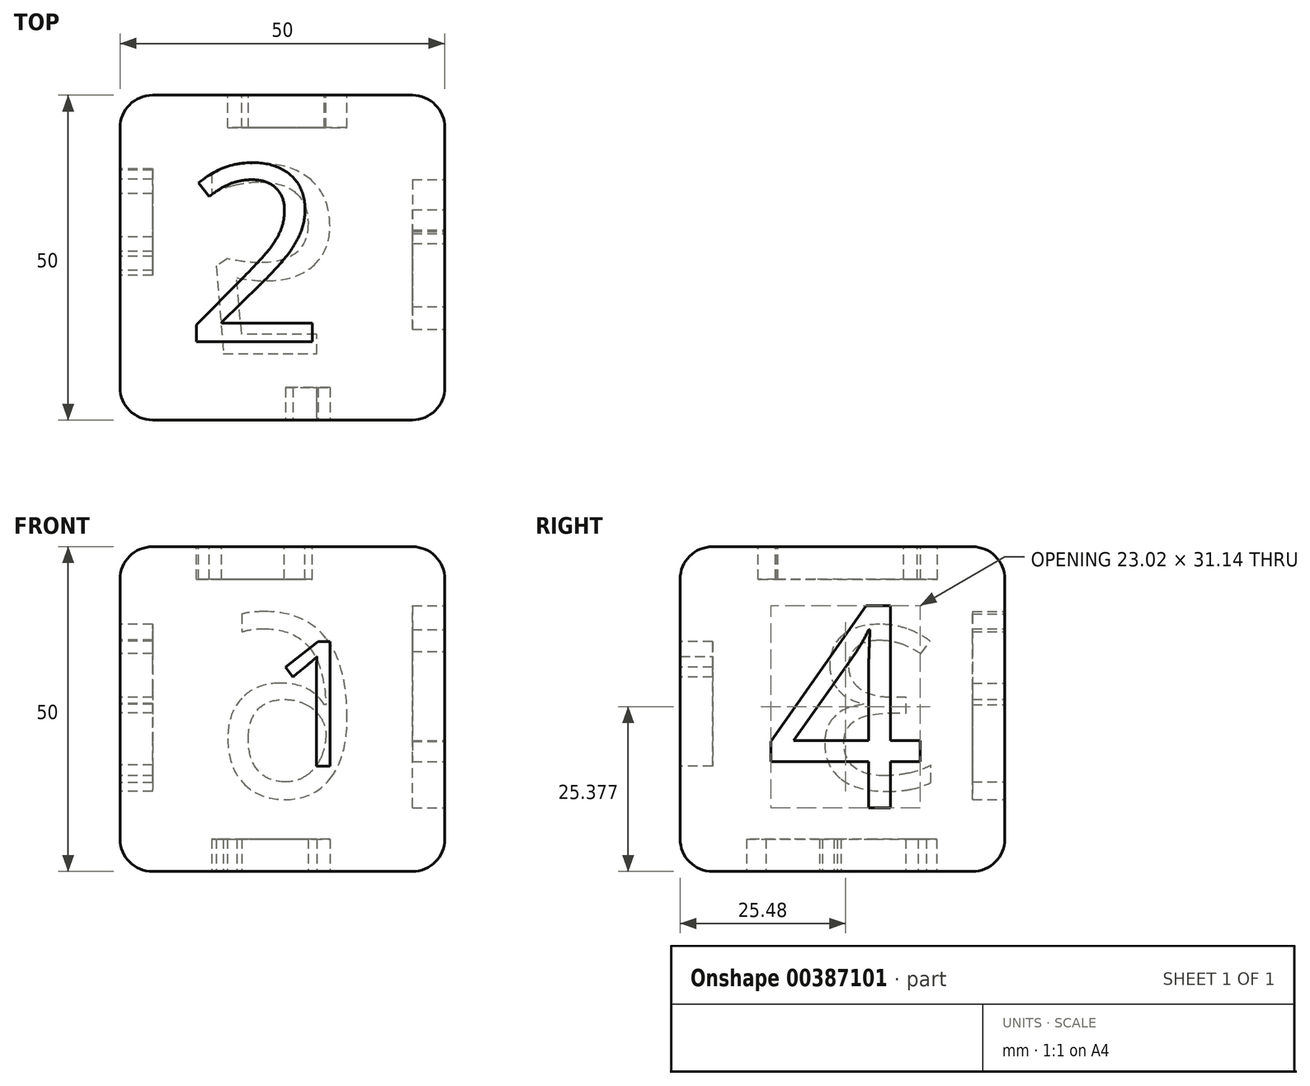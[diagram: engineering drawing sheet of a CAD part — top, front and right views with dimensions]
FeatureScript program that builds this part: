
annotation { "Feature Type Name" : "Feature", "Feature Type Description" : "" }
export const myFeature = defineFeature(function(context is Context, id is Id, definition is map)
    precondition{}
    {
        {
            var Q0;
            Q0=qCreatedBy(makeId("Front.planeOp"),FACE);
            var sketch = newSketch(context, id + "F0", { "sketchPlane" : qUnion([Q0])});
            skLineSegment(sketch, "E0.bottom", {"start": v(-34.08, 35.65) * mm, "end": v(15.92, 35.65) * mm});
            skLineSegment(sketch, "E0.top", {"start": v(-34.08, -14.35) * mm, "end": v(15.92, -14.35) * mm});
            skLineSegment(sketch, "E0.left", {"start": v(-34.08, 35.65) * mm, "end": v(-34.08, -14.35) * mm});
            skLineSegment(sketch, "E0.right", {"start": v(15.92, 35.65) * mm, "end": v(15.92, -14.35) * mm});
            skSolve(sketch);
        }
        {
            var Q0;
            Q0=makeQuery(id+"F0.imprint","IMPRINT",FACE,{"disambiguationData":[TD([[makeQuery(id+"F0.imprint","IMPRINT",EDGE,{"derivedFrom":sQuery(id+"F0.wireOp",EDGE,"E0.bottom")}),-1.0]])]});
            extrude(context, id + "F1", {"entities" : qUnion([Q0]), "depth" : 50 * mm});
        }
        {
            var Q0;
            Q0=makeQuery(id+"F1.opExtrude","CAP_FACE",FACE,{"disambiguationData":[OSD([sQuery(id+"F0.wireOp",EDGE,"E0.bottom"),sQuery(id+"F0.wireOp",EDGE,"E0.top"),sQuery(id+"F0.wireOp",EDGE,"E0.left"),sQuery(id+"F0.wireOp",EDGE,"E0.right")])],"isStart":false});
            var Q1;
            Q1=makeQuery(id+"F1.opExtrude","SWEPT_FACE",FACE,{"disambiguationData":[OSD([sQuery(id+"F0.wireOp",EDGE,"E0.right")])]});
            var Q2;
            Q2=makeQuery(id+"F1.opExtrude","CAP_EDGE",EDGE,{"disambiguationData":[OSD([sQuery(id+"F0.wireOp",EDGE,"E0.right")])],"isStart":true});
            var Q3;
            Q3=makeQuery(id+"F1.opExtrude","SWEPT_FACE",FACE,{"disambiguationData":[OSD([sQuery(id+"F0.wireOp",EDGE,"E0.bottom")])]});
            var Q4;
            Q4=makeQuery(id+"F1.opExtrude","CAP_FACE",FACE,{"disambiguationData":[OSD([sQuery(id+"F0.wireOp",EDGE,"E0.bottom"),sQuery(id+"F0.wireOp",EDGE,"E0.top"),sQuery(id+"F0.wireOp",EDGE,"E0.left"),sQuery(id+"F0.wireOp",EDGE,"E0.right")])],"isStart":true});
            var Q5;
            Q5=makeQuery(id+"F1.opExtrude","SWEPT_FACE",FACE,{"disambiguationData":[OSD([sQuery(id+"F0.wireOp",EDGE,"E0.left")])]});
            var Q6;
            Q6=makeQuery(id+"F1.opExtrude","SWEPT_FACE",FACE,{"disambiguationData":[OSD([sQuery(id+"F0.wireOp",EDGE,"E0.top")])]});
            fillet(context, id + "F2", {"entities" : qUnion([Q0, Q1, Q2, Q3, Q4, Q5, Q6]), "radius" : 5 * mm, "tangentPropagation" : true, "allowEdgeOverflow" : false});
        }
        {
            var Q0;
            Q0=makeQuery(id+"F1.opExtrude","CAP_FACE",FACE,{"disambiguationData":[OSD([sQuery(id+"F0.wireOp",EDGE,"E0.bottom"),sQuery(id+"F0.wireOp",EDGE,"E0.top"),sQuery(id+"F0.wireOp",EDGE,"E0.left"),sQuery(id+"F0.wireOp",EDGE,"E0.right")])],"isStart":false});
            var sketch = newSketch(context, id + "F3", { "sketchPlane" : qUnion([Q0])});
            skText(sketch, "E1", { "text": "1", "fontName": "OpenSans-Regular.ttf"});
            const initialGuessF3  = {"E1": [-0.0111, 0.00188, 1, 0, 0.0193]};
            skSetInitialGuess(sketch, initialGuessF3);
            skSolve(sketch);
        }
        {
            var Q0;
            Q0 = qSketchRegion(id + "F3", true);
            extrude(context, id + "F4", {"entities" : qUnion([Q0]), "operationType" : NewBodyOperationType.REMOVE, "oppositeDirection" : true, "depth" : 5 * mm});
        }
        {
            var Q0;
            Q0=makeQuery(id+"F1.opExtrude","CAP_FACE",FACE,{"disambiguationData":[OSD([sQuery(id+"F0.wireOp",EDGE,"E0.bottom"),sQuery(id+"F0.wireOp",EDGE,"E0.top"),sQuery(id+"F0.wireOp",EDGE,"E0.left"),sQuery(id+"F0.wireOp",EDGE,"E0.right")])],"isStart":true});
            var sketch = newSketch(context, id + "F5", { "sketchPlane" : qUnion([Q0])});
            skText(sketch, "E2", { "text": "6", "fontName": "OpenSans-Regular.ttf"});
            const initialGuessF5  = {"E2": [-0.00313, -0.00289, 1, 0, 0.02839]};
            skSetInitialGuess(sketch, initialGuessF5);
            skSolve(sketch);
        }
        {
            var Q0;
            Q0 = qSketchRegion(id + "F5", true);
            extrude(context, id + "F6", {"entities" : qUnion([Q0]), "operationType" : NewBodyOperationType.REMOVE, "oppositeDirection" : true, "depth" : 5 * mm});
        }
        {
            var Q0;
            Q0=makeQuery(id+"F1.opExtrude","SWEPT_FACE",FACE,{"disambiguationData":[OSD([sQuery(id+"F0.wireOp",EDGE,"E0.bottom")])]});
            var sketch = newSketch(context, id + "F7", { "sketchPlane" : qUnion([Q0])});
            skText(sketch, "E3", { "text": "2", "fontName": "OpenSans-Regular.ttf"});
            const initialGuessF7  = {"E3": [-0.0242, -0.03797, 1, 0, 0.02745]};
            skSetInitialGuess(sketch, initialGuessF7);
            skSolve(sketch);
        }
        {
            var Q0;
            Q0 = qSketchRegion(id + "F7", true);
            extrude(context, id + "F8", {"entities" : qUnion([Q0]), "operationType" : NewBodyOperationType.REMOVE, "oppositeDirection" : true, "depth" : 5 * mm});
        }
        {
            var Q0;
            Q0=makeQuery(id+"F1.opExtrude","SWEPT_FACE",FACE,{"disambiguationData":[OSD([sQuery(id+"F0.wireOp",EDGE,"E0.top")])]});
            var sketch = newSketch(context, id + "F9", { "sketchPlane" : qUnion([Q0])});
            skText(sketch, "E4", { "text": "5", "fontName": "OpenSans-Regular.ttf"});
            const initialGuessF9  = {"E4": [-0.02258, 0.01092, 1, 0, 0.02913]};
            skSetInitialGuess(sketch, initialGuessF9);
            skSolve(sketch);
        }
        {
            var Q0;
            Q0 = qSketchRegion(id + "F9", true);
            extrude(context, id + "F10", {"entities" : qUnion([Q0]), "operationType" : NewBodyOperationType.REMOVE, "oppositeDirection" : true, "depth" : 5 * mm});
        }
        {
            var Q0;
            Q0=makeQuery(id+"F1.opExtrude","SWEPT_FACE",FACE,{"disambiguationData":[OSD([sQuery(id+"F0.wireOp",EDGE,"E0.left")])]});
            var sketch = newSketch(context, id + "F11", { "sketchPlane" : qUnion([Q0])});
            skText(sketch, "E5", { "text": "3", "fontName": "OpenSans-Regular.ttf"});
            const initialGuessF11  = {"E5": [0.00975, -0.00167, 1, 0, 0.02523]};
            skSetInitialGuess(sketch, initialGuessF11);
            skSolve(sketch);
        }
        {
            var Q0;
            Q0 = qSketchRegion(id + "F11", true);
            extrude(context, id + "F12", {"entities" : qUnion([Q0]), "operationType" : NewBodyOperationType.REMOVE, "oppositeDirection" : true, "depth" : 5 * mm});
        }
        {
            var Q0;
            Q0=makeQuery(id+"F1.opExtrude","SWEPT_FACE",FACE,{"disambiguationData":[OSD([sQuery(id+"F0.wireOp",EDGE,"E0.right")])]});
            var sketch = newSketch(context, id + "F13", { "sketchPlane" : qUnion([Q0])});
            skText(sketch, "E6", { "text": "4", "fontName": "OpenSans-Regular.ttf"});
            const initialGuessF13  = {"E6": [-0.03694, -0.00454, 1, 0, 0.03123]};
            skSetInitialGuess(sketch, initialGuessF13);
            skSolve(sketch);
        }
        {
            var Q0;
            Q0 = qSketchRegion(id + "F13", true);
            extrude(context, id + "F14", {"entities" : qUnion([Q0]), "operationType" : NewBodyOperationType.REMOVE, "oppositeDirection" : true, "depth" : 5 * mm});
        }
    });
